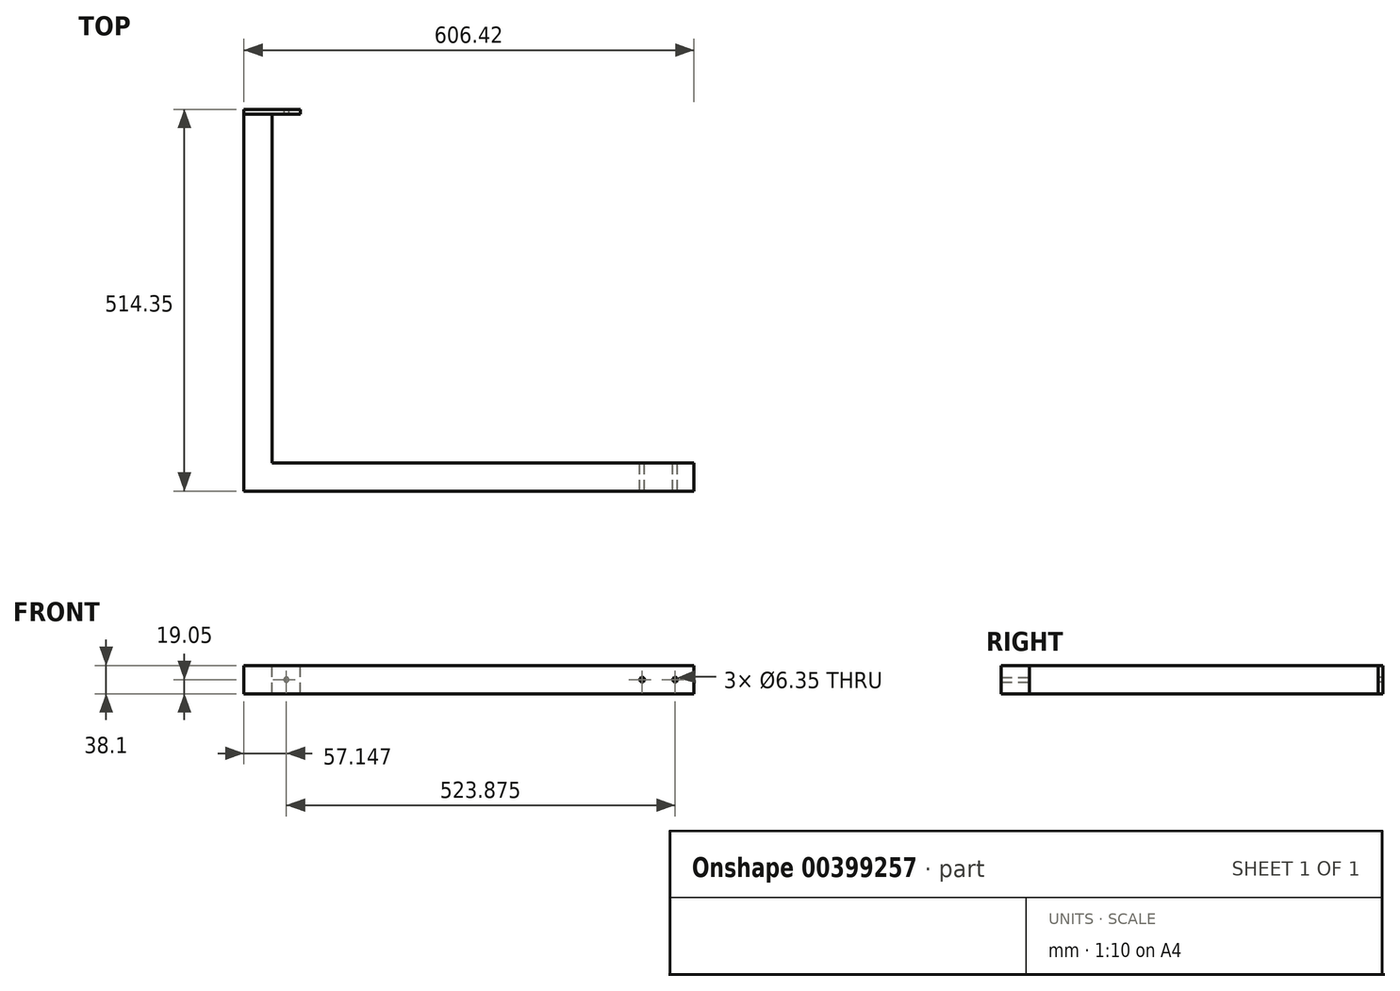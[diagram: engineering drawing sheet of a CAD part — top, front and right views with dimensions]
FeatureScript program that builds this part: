
annotation { "Feature Type Name" : "Feature", "Feature Type Description" : "" }
export const myFeature = defineFeature(function(context is Context, id is Id, definition is map)
    precondition{}
    {
        {
            var Q0;
            Q0=qCreatedBy(makeId("Top.planeOp"),FACE);
            var sketch = newSketch(context, id + "F0", { "sketchPlane" : qUnion([Q0])});
            skLineSegment(sketch, "E0.bottom", {"start": v(-303.21, -254) * mm, "end": v(303.21, -254) * mm});
            skLineSegment(sketch, "E0.top", {"start": v(-303.21, 254) * mm, "end": v(303.21, 254) * mm});
            skLineSegment(sketch, "E0.left", {"start": v(-303.21, -254) * mm, "end": v(-303.21, 254) * mm});
            skLineSegment(sketch, "E0.right", {"start": v(303.21, -254) * mm, "end": v(303.21, 254) * mm});
            skPoint(sketch, "E0.middle", {"position": v(0, 0) * mm});
            skSolve(sketch);
        }
        {
            var Q0;
            Q0=makeQuery(id+"F0.imprint","IMPRINT",FACE,{"disambiguationData":[TD([[makeQuery(id+"F0.imprint","IMPRINT",EDGE,{"derivedFrom":sQuery(id+"F0.wireOp",EDGE,"E0.bottom")}),1.0]])]});
            extrude(context, id + "F1", {"entities" : qUnion([Q0]), "depth" : 38.1 * mm});
        }
        {
            var Q0;
            Q0=makeQuery(id+"F1.opExtrude","CAP_FACE",FACE,{"disambiguationData":[OSD([sQuery(id+"F0.wireOp",EDGE,"E0.bottom"),sQuery(id+"F0.wireOp",EDGE,"E0.top"),sQuery(id+"F0.wireOp",EDGE,"E0.left"),sQuery(id+"F0.wireOp",EDGE,"E0.right")])],"isStart":false});
            var sketch = newSketch(context, id + "F2", { "sketchPlane" : qUnion([Q0])});
            skLineSegment(sketch, "E1.bottom", {"start": v(303.21, 254) * mm, "end": v(-265.11, 254) * mm});
            skLineSegment(sketch, "E1.top", {"start": v(303.21, -215.9) * mm, "end": v(-265.11, -215.9) * mm});
            skLineSegment(sketch, "E1.left", {"start": v(303.21, 254) * mm, "end": v(303.21, -215.9) * mm});
            skLineSegment(sketch, "E1.right", {"start": v(-265.11, 254) * mm, "end": v(-265.11, -215.9) * mm});
            skSolve(sketch);
        }
        {
            var Q0;
            Q0 = qSketchRegion(id + "F2", true);
            extrude(context, id + "F3", {"entities" : qUnion([Q0]), "operationType" : NewBodyOperationType.REMOVE, "endBound" : BoundingType.THROUGH_ALL, "oppositeDirection" : true, "depth" : 25.4 * mm});
        }
        {
            var Q0;
            Q0=makeQuery(id+"F3.boolean.opBoolean","COPY",FACE,{"derivedFrom":makeQuery(id+"F3.opExtrude","SWEPT_FACE",FACE,{"disambiguationData":[OSD([sQuery(id+"F2.wireOp",EDGE,"E1.top")])]})});
            var sketch = newSketch(context, id + "F4", { "sketchPlane" : qUnion([Q0])});
            skCircle(sketch, "E2", {"center": v(-277.81, 19.05) * mm, "radius": 3.18 * mm});
            skPoint(sketch, "E2.centerSnap0", {"position": v(-303.21, 19.05) * mm});
            skCircle(sketch, "E3", {"center": v(-233.36, 19.05) * mm, "radius": 3.18 * mm});
            skSolve(sketch);
        }
        {
            var Q0;
            Q0 = qSketchRegion(id + "F4", true);
            extrude(context, id + "F5", {"entities" : qUnion([Q0]), "operationType" : NewBodyOperationType.REMOVE, "endBound" : BoundingType.THROUGH_ALL, "oppositeDirection" : true, "depth" : 25.4 * mm});
        }
        {
            var Q0;
            Q0=makeQuery(id+"F1.opExtrude","SWEPT_FACE",FACE,{"disambiguationData":[OSD([sQuery(id+"F0.wireOp",EDGE,"E0.top")])]});
            var sketch = newSketch(context, id + "F6", { "sketchPlane" : qUnion([Q0])});
            skLineSegment(sketch, "E4.bottom", {"start": v(227.01, 0) * mm, "end": v(303.21, 0) * mm});
            skLineSegment(sketch, "E4.top", {"start": v(227.01, 38.1) * mm, "end": v(303.21, 38.1) * mm});
            skLineSegment(sketch, "E4.left", {"start": v(227.01, 0) * mm, "end": v(227.01, 38.1) * mm});
            skLineSegment(sketch, "E4.right", {"start": v(303.21, 0) * mm, "end": v(303.21, 38.1) * mm});
            skSolve(sketch);
        }
        {
            var Q0;
            Q0 = qSketchRegion(id + "F6", true);
            extrude(context, id + "F7", {"entities" : qUnion([Q0]), "depth" : 6.35 * mm});
        }
        {
            var Q0;
            Q0=makeQuery(id+"F7.opExtrude","CAP_FACE",FACE,{"disambiguationData":[OSD([sQuery(id+"F6.wireOp",EDGE,"E4.bottom"),sQuery(id+"F6.wireOp",EDGE,"E4.top"),sQuery(id+"F6.wireOp",EDGE,"E4.left"),sQuery(id+"F6.wireOp",EDGE,"E4.right")])],"isStart":true});
            var sketch = newSketch(context, id + "F8", { "sketchPlane" : qUnion([Q0])});
            skCircle(sketch, "E5", {"center": v(-246.06, 19.05) * mm, "radius": 3.18 * mm});
            skPoint(sketch, "E5.centerSnap0", {"position": v(-227.01, 19.05) * mm});
            skSolve(sketch);
        }
        {
            var Q0;
            Q0 = qSketchRegion(id + "F8", true);
            extrude(context, id + "F9", {"entities" : qUnion([Q0]), "operationType" : NewBodyOperationType.REMOVE, "endBound" : BoundingType.THROUGH_ALL, "oppositeDirection" : true, "depth" : 25.4 * mm});
        }
    });
